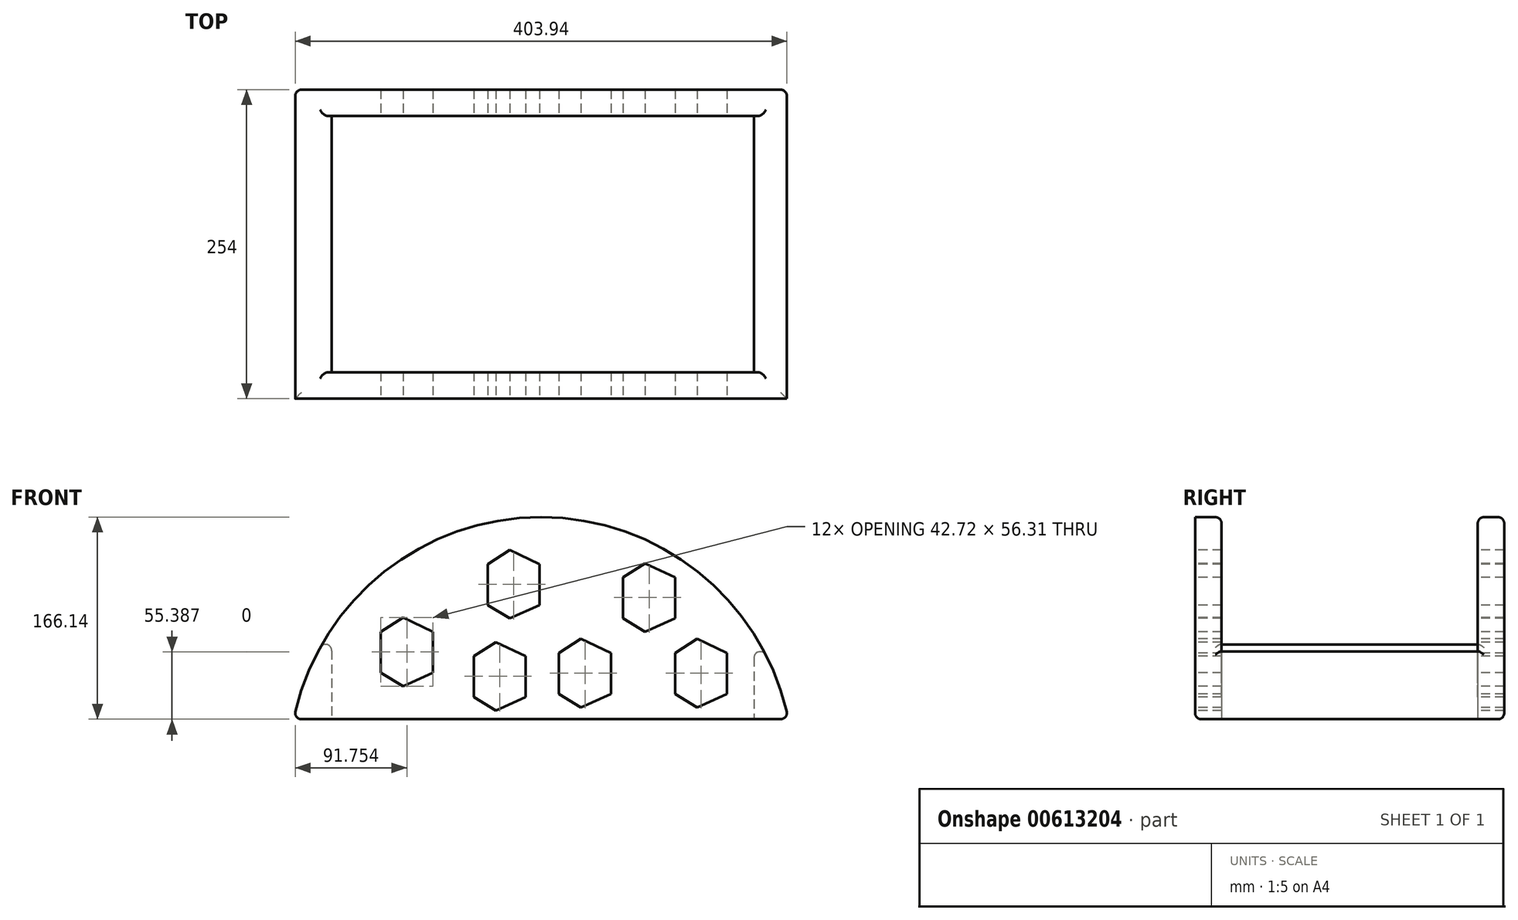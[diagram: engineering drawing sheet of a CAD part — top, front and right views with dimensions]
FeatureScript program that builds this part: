
annotation { "Feature Type Name" : "Feature", "Feature Type Description" : "" }
export const myFeature = defineFeature(function(context is Context, id is Id, definition is map)
    precondition{}
    {
        {
            var Q0;
            Q0=qCreatedBy(makeId("Front.planeOp"),FACE);
            var sketch = newSketch(context, id + "F0", { "sketchPlane" : qUnion([Q0])});
            skLineSegment(sketch, "E0", {"start": v(-203.2, 0) * mm, "end": v(203.2, 0) * mm});
            skArc(sketch, "E1", {"start": v(203.2, 0) * mm, "mid": v(0, 166.14) * mm, "end": v(-203.2, 0) * mm});
            skSolve(sketch);
        }
        {
            var Q0;
            Q0=makeQuery(id+"F0.imprint","IMPRINT",FACE,{"disambiguationData":[TD([[makeQuery(id+"F0.imprint","IMPRINT",EDGE,{"derivedFrom":sQuery(id+"F0.wireOp",EDGE,"E0")}),1.0]])]});
            extrude(context, id + "F1", {"entities" : qUnion([Q0]), "depth" : 254 * mm, "offsetDistance" : 25.4 * mm});
        }
        {
            var Q0;
            Q0=makeQuery(id+"F1.opExtrude","CAP_FACE",FACE,{"disambiguationData":[OSD([sQuery(id+"F0.wireOp",EDGE,"E0"),sQuery(id+"F0.wireOp",EDGE,"E1")])],"isStart":false});
            var sketch = newSketch(context, id + "F2", { "sketchPlane" : qUnion([Q0])});
            skLineSegment(sketch, "E2", {"start": v(-131.57, 38.24) * mm, "end": v(-131.57, 71.9) * mm});
            skLineSegment(sketch, "E3", {"start": v(-131.57, 38.24) * mm, "end": v(-113.45, 27.23) * mm});
            skLineSegment(sketch, "E4", {"start": v(-113.45, 27.23) * mm, "end": v(-88.86, 38.24) * mm});
            skLineSegment(sketch, "E5", {"start": v(-88.86, 71.9) * mm, "end": v(-88.86, 38.24) * mm});
            skLineSegment(sketch, "E6", {"start": v(-88.86, 71.9) * mm, "end": v(-113.45, 83.54) * mm});
            skLineSegment(sketch, "E7", {"start": v(-113.45, 83.54) * mm, "end": v(-131.57, 71.9) * mm});
            skLineSegment(sketch, "E8", {"start": v(-43.87, 93.84) * mm, "end": v(-43.87, 127.5) * mm});
            skLineSegment(sketch, "E9", {"start": v(-43.87, 93.84) * mm, "end": v(-25.75, 82.83) * mm});
            skLineSegment(sketch, "E10", {"start": v(-25.75, 82.83) * mm, "end": v(-1.16, 93.84) * mm});
            skLineSegment(sketch, "E11", {"start": v(-1.16, 127.5) * mm, "end": v(-1.16, 93.84) * mm});
            skLineSegment(sketch, "E12", {"start": v(-1.16, 127.5) * mm, "end": v(-25.75, 139.14) * mm});
            skLineSegment(sketch, "E13", {"start": v(-25.75, 139.14) * mm, "end": v(-43.87, 127.5) * mm});
            skLineSegment(sketch, "E14", {"start": v(67.46, 82.83) * mm, "end": v(67.46, 116.49) * mm});
            skLineSegment(sketch, "E15", {"start": v(67.46, 82.83) * mm, "end": v(85.59, 71.83) * mm});
            skLineSegment(sketch, "E16", {"start": v(85.59, 71.83) * mm, "end": v(110.18, 82.83) * mm});
            skLineSegment(sketch, "E17", {"start": v(110.18, 116.49) * mm, "end": v(110.18, 82.83) * mm});
            skLineSegment(sketch, "E18", {"start": v(110.18, 116.49) * mm, "end": v(85.59, 128.14) * mm});
            skLineSegment(sketch, "E19", {"start": v(85.59, 128.14) * mm, "end": v(67.46, 116.49) * mm});
            skLineSegment(sketch, "E20", {"start": v(14.73, 20.7) * mm, "end": v(14.73, 54.36) * mm});
            skLineSegment(sketch, "E21", {"start": v(14.73, 20.7) * mm, "end": v(32.85, 9.7) * mm});
            skLineSegment(sketch, "E22", {"start": v(32.85, 9.7) * mm, "end": v(57.45, 20.7) * mm});
            skLineSegment(sketch, "E23", {"start": v(57.45, 54.36) * mm, "end": v(57.45, 20.7) * mm});
            skLineSegment(sketch, "E24", {"start": v(57.45, 54.36) * mm, "end": v(32.85, 66.01) * mm});
            skLineSegment(sketch, "E25", {"start": v(32.85, 66.01) * mm, "end": v(14.73, 54.36) * mm});
            skLineSegment(sketch, "E26", {"start": v(-55.35, 18.15) * mm, "end": v(-55.35, 51.8) * mm});
            skLineSegment(sketch, "E27", {"start": v(-55.35, 18.15) * mm, "end": v(-37.23, 7.14) * mm});
            skLineSegment(sketch, "E28", {"start": v(-37.23, 7.14) * mm, "end": v(-12.63, 18.15) * mm});
            skLineSegment(sketch, "E29", {"start": v(-12.63, 51.8) * mm, "end": v(-12.63, 18.15) * mm});
            skLineSegment(sketch, "E30", {"start": v(-12.63, 51.8) * mm, "end": v(-37.23, 63.45) * mm});
            skLineSegment(sketch, "E31", {"start": v(-37.23, 63.45) * mm, "end": v(-55.35, 51.8) * mm});
            skLineSegment(sketch, "E32", {"start": v(110.18, 20.7) * mm, "end": v(110.18, 54.36) * mm});
            skLineSegment(sketch, "E33", {"start": v(110.18, 20.7) * mm, "end": v(128.3, 9.7) * mm});
            skLineSegment(sketch, "E34", {"start": v(128.3, 9.7) * mm, "end": v(152.9, 20.7) * mm});
            skLineSegment(sketch, "E35", {"start": v(152.9, 54.36) * mm, "end": v(152.9, 20.7) * mm});
            skLineSegment(sketch, "E36", {"start": v(152.9, 54.36) * mm, "end": v(128.3, 66.01) * mm});
            skLineSegment(sketch, "E37", {"start": v(128.3, 66.01) * mm, "end": v(110.18, 54.36) * mm});
            skSolve(sketch);
        }
        {
            var Q0;
            Q0=makeQuery(id+"F1.opExtrude","SWEPT_FACE",FACE,{"disambiguationData":[OSD([sQuery(id+"F0.wireOp",EDGE,"E0")])]});
            var sketch = newSketch(context, id + "F3", { "sketchPlane" : qUnion([Q0])});
            skPoint(sketch, "E38", {"position": v(203.2, 127) * mm});
            skPoint(sketch, "E39", {"position": v(-203.2, 127) * mm});
            skLineSegment(sketch, "E40", {"start": v(175.1, 21.74) * mm, "end": v(175.1, 232.26) * mm});
            skPoint(sketch, "E41", {"position": v(0, 254) * mm});
            skLineSegment(sketch, "E42", {"start": v(175.1, 232.26) * mm, "end": v(-172.03, 232.26) * mm});
            skLineSegment(sketch, "E43", {"start": v(175.1, 21.74) * mm, "end": v(-172.03, 21.74) * mm});
            skLineSegment(sketch, "E44", {"start": v(-172.03, 21.74) * mm, "end": v(-172.03, 232.26) * mm});
            skSolve(sketch);
        }
        {
            var Q0;
            Q0 = qSketchRegion(id + "F3", true);
            extrude(context, id + "F4", {"entities" : qUnion([Q0]), "operationType" : NewBodyOperationType.REMOVE, "oppositeDirection" : true, "depth" : 508 * mm, "offsetDistance" : 25.4 * mm});
        }
        {
            var Q0;
            Q0 = qSketchRegion(id + "F2", true);
            extrude(context, id + "F5", {"entities" : qUnion([Q0]), "operationType" : NewBodyOperationType.REMOVE, "oppositeDirection" : true, "depth" : 508 * mm, "offsetDistance" : 25.4 * mm});
        }
        {
            var Q0;
            Q0=makeQuery(id+"F4.boolean.opBoolean","INTERSECT",EDGE,{"derivedFrom":[makeQuery(id+"F1.opExtrude","SWEPT_FACE",FACE,{"disambiguationData":[OSD([sQuery(id+"F0.wireOp",EDGE,"E1")])]}),makeQuery(id+"F4.opExtrude","SWEPT_FACE",FACE,{"disambiguationData":[OSD([sQuery(id+"F3.wireOp",EDGE,"E42")])]})]});
            var Q1;
            Q1=makeQuery(id+"F4.boolean.opBoolean","INTERSECT",EDGE,{"derivedFrom":[makeQuery(id+"F1.opExtrude","SWEPT_FACE",FACE,{"disambiguationData":[OSD([sQuery(id+"F0.wireOp",EDGE,"E1")])]}),makeQuery(id+"F4.opExtrude","SWEPT_FACE",FACE,{"disambiguationData":[OSD([sQuery(id+"F3.wireOp",EDGE,"E44")])]})]});
            var Q2;
            Q2=makeQuery(id+"F4.boolean.opBoolean","INTERSECT",EDGE,{"derivedFrom":[makeQuery(id+"F1.opExtrude","SWEPT_FACE",FACE,{"disambiguationData":[OSD([sQuery(id+"F0.wireOp",EDGE,"E1")])]}),makeQuery(id+"F4.opExtrude","SWEPT_FACE",FACE,{"disambiguationData":[OSD([sQuery(id+"F3.wireOp",EDGE,"E43")])]})]});
            var Q3;
            Q3=makeQuery(id+"F1.opExtrude","CAP_EDGE",EDGE,{"disambiguationData":[OSD([sQuery(id+"F0.wireOp",EDGE,"E1")])],"isStart":true});
            var Q4;
            Q4=makeQuery(id+"F1.opExtrude","CAP_EDGE",EDGE,{"disambiguationData":[OSD([sQuery(id+"F0.wireOp",EDGE,"E0")])],"isStart":true});
            var Q5;
            Q5=makeQuery(id+"F1.opExtrude","CAP_EDGE",EDGE,{"disambiguationData":[OSD([sQuery(id+"F0.wireOp",EDGE,"E0")])],"isStart":false});
            var Q6;
            Q6=makeQuery(id+"F4.boolean.opBoolean","COPY",EDGE,{"derivedFrom":makeQuery(id+"F4.opExtrude","CAP_EDGE",EDGE,{"disambiguationData":[OSD([sQuery(id+"F3.wireOp",EDGE,"E40")])],"isStart":true})});
            var Q7;
            {var subQ0=sQuery(id+"F0.wireOp",EDGE,"E1");var subQ1=sQuery(id+"F0.wireOp",EDGE,"E0");Q7=makeQuery(id+"F1.opExtrude","SWEPT_EDGE",EDGE,{"disambiguationData":[OSD([subQ1,subQ0]),TDD([makeQuery(id+"F0.imprint","INTERSECT",VERTEX,{"disambiguationData":[OD(1.0)],"derivedFrom":[subQ1,subQ0]})])]});}
            var Q8;
            Q8=makeQuery(id+"F4.boolean.opBoolean","COPY",EDGE,{"derivedFrom":makeQuery(id+"F4.opExtrude","CAP_EDGE",EDGE,{"disambiguationData":[OSD([sQuery(id+"F3.wireOp",EDGE,"E42")])],"isStart":true})});
            var Q9;
            Q9=makeQuery(id+"F4.boolean.opBoolean","COPY",EDGE,{"derivedFrom":makeQuery(id+"F4.opExtrude","CAP_EDGE",EDGE,{"disambiguationData":[OSD([sQuery(id+"F3.wireOp",EDGE,"E44")])],"isStart":true})});
            var Q10;
            {var subQ0=sQuery(id+"F0.wireOp",EDGE,"E1");var subQ1=sQuery(id+"F0.wireOp",EDGE,"E0");Q10=makeQuery(id+"F1.opExtrude","SWEPT_EDGE",EDGE,{"disambiguationData":[OSD([subQ1,subQ0]),TDD([makeQuery(id+"F0.imprint","INTERSECT",VERTEX,{"disambiguationData":[OD(0.0)],"derivedFrom":[subQ1,subQ0]})])]});}
            var Q11;
            Q11=makeQuery(id+"F4.boolean.opBoolean","INTERSECT",EDGE,{"derivedFrom":[makeQuery(id+"F1.opExtrude","SWEPT_FACE",FACE,{"disambiguationData":[OSD([sQuery(id+"F0.wireOp",EDGE,"E1")])]}),makeQuery(id+"F4.opExtrude","SWEPT_FACE",FACE,{"disambiguationData":[OSD([sQuery(id+"F3.wireOp",EDGE,"E40")])]})]});
            var Q12;
            Q12=makeQuery(id+"F4.boolean.opBoolean","COPY",EDGE,{"derivedFrom":makeQuery(id+"F4.opExtrude","CAP_EDGE",EDGE,{"disambiguationData":[OSD([sQuery(id+"F3.wireOp",EDGE,"E43")])],"isStart":true})});
            fillet(context, id + "F6", {"entities" : qUnion([Q0, Q1, Q2, Q3, Q4, Q5, Q6, Q7, Q8, Q9, Q10, Q11, Q12]), "radius" : 5.08 * mm, "tangentPropagation" : true, "allowEdgeOverflow" : false});
        }
    });
